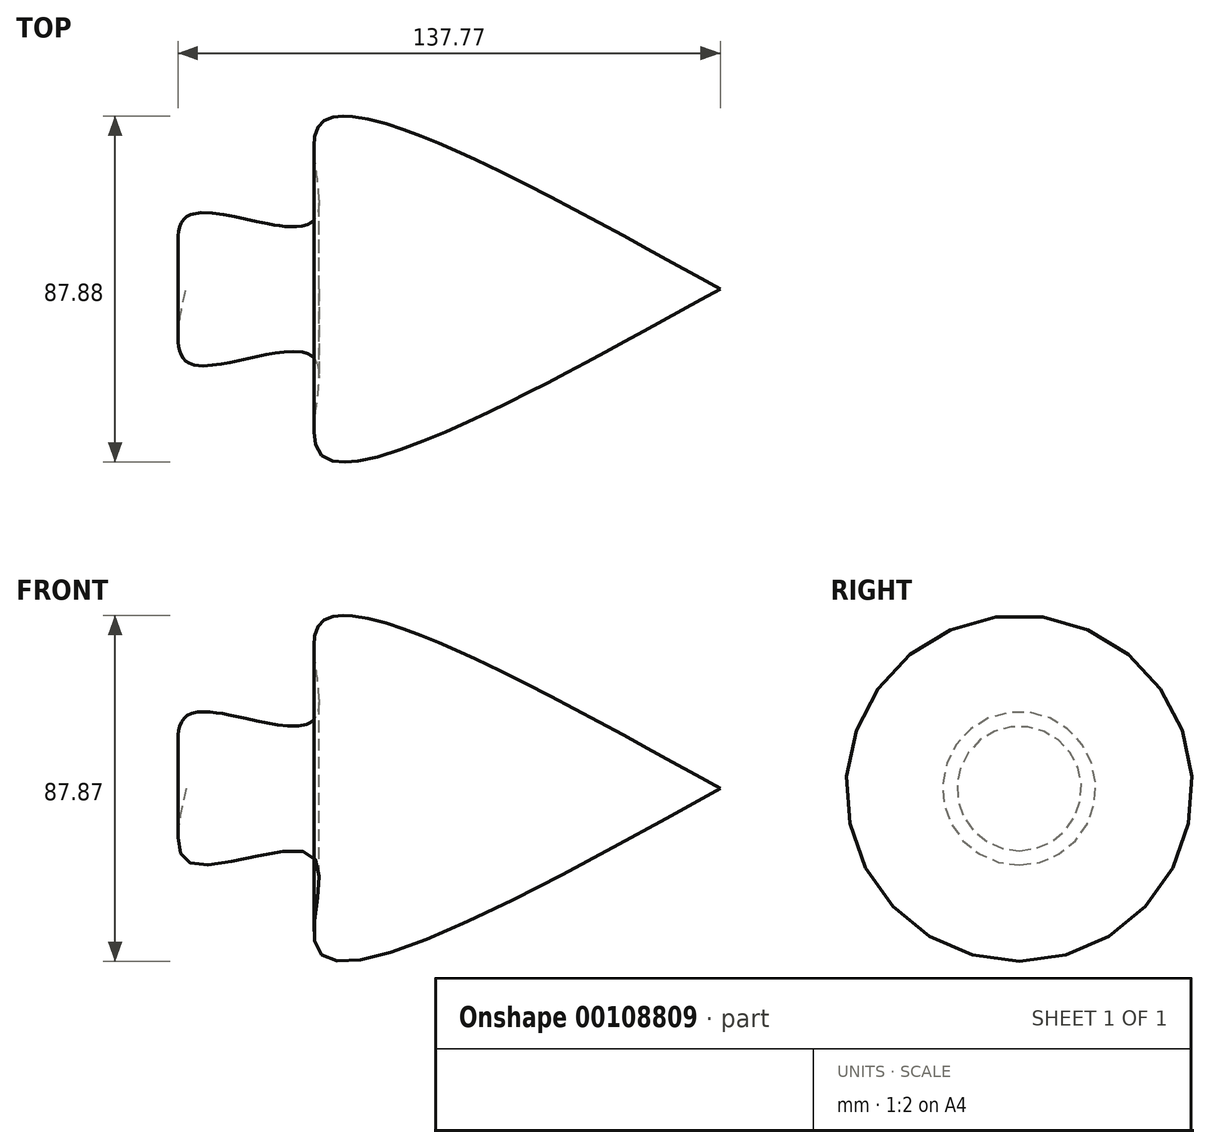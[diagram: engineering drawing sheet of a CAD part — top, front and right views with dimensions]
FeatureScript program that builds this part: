
annotation { "Feature Type Name" : "Feature", "Feature Type Description" : "" }
export const myFeature = defineFeature(function(context is Context, id is Id, definition is map)
    precondition{}
    {
        {
            var Q0;
            Q0=qCreatedBy(makeId("Front.planeOp"),FACE);
            var sketch = newSketch(context, id + "F0", { "sketchPlane" : qUnion([Q0])});
            skFitSpline(sketch, "E0", {"points": [v(-65.03, 0) * mm, v(-63.52, -19.1) * mm, v(-32.91, -17.1) * mm, v(-31.66, -40.84) * mm, v(70.72, 0) * mm], "startDerivative": vector(-33.98, -150.02) * mm, "endDerivative": vector(347.3, 192.08) * mm});
            skLineSegment(sketch, "E1", {"start": v(-65.03, 0) * mm, "end": v(70.72, 0) * mm});
            skSolve(sketch);
        }
        {
            var Q0;
            Q0 = qSketchRegion(id + "F0", true);
            var Q1;
            Q1=sQuery(id+"F0.wireOp",EDGE,"E1");
            revolve(context, id + "F1", {"entities" : qUnion([Q0]), "axis" : qUnion([Q1]), "revolveType" : RevolveType.FULL});
        }
    });
